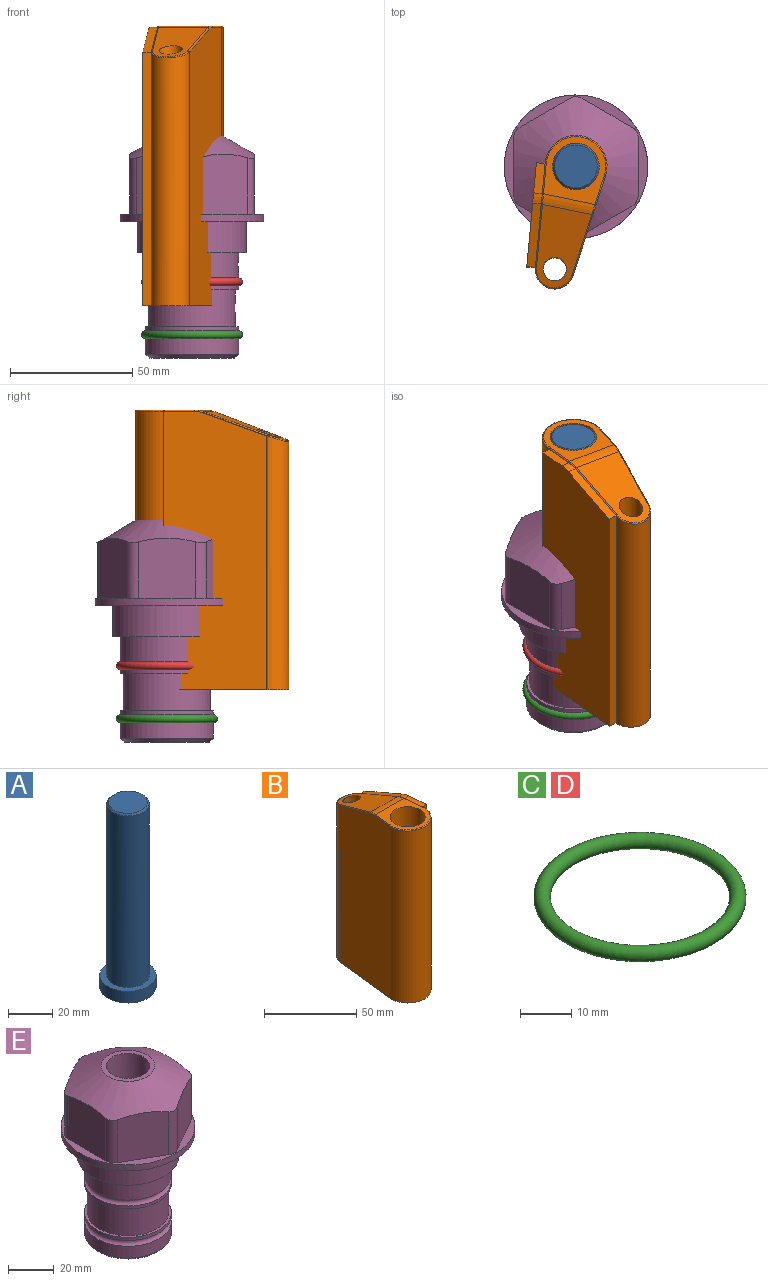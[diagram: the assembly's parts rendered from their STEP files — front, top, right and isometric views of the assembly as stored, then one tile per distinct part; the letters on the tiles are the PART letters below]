
ASSEMBLY  parts=5 mates=3
PART A: 6 faces, bbox 25.4x25.4x101.6 mm
  f0: plane 17.46x17.46mm, normal (0,0,1), area 239.5mm2, adj f5
  f1: plane 25.4x25.4mm, normal (0,0,-1), area 506.7mm2, adj f2
  f2: cylinder r=12.7mm len=25.4mm, axis (0,0,1), area 506.7mm2, adj f1,f3
  f3: plane 25.4x25.4mm, normal (0,0,1), area 221.7mm2, adj f2,f4
  f4: cylinder r=9.53mm len=94.46mm, axis (0,0,1), area 5653mm2, adj f3,f5
  f5: cone r=8.73mm half-angle=45deg, axis (0,0,-1), area 64.4mm2, adj f0,f4
PART B: 49 faces, bbox 29.9x64.5x114.4 mm
  f0: cylinder r=12.7mm len=113.87mm, axis (0,0,-1), area 4865.2mm2, adj f2,f10,f16,f47
  f1: cylinder r=7.94mm len=103.71mm, axis (0,0,-1), area 2367.2mm2, adj f2,f13,f16,f43
  f2: plane 113.87x42.33mm, normal (-0.99,0.11,0), area 4707.7mm2, adj f0,f1,f12,f14,f15,f16
  f3: cylinder r=9.53mm len=114.38mm, axis (0,0,-1), area 6845.2mm2, adj f5,f16
  f4: cylinder r=4.76mm len=106.31mm, axis (0,0,-1), area 3128.7mm2, adj f6,f16
  f5: plane 25.83x24.38mm, normal (0,0,1), area 262.2mm2, adj f3,f7,f8,f10,f12
  f6: plane 32.49x20.55mm, normal (0,0.34,0.94), area 489.9mm2, adj f4,f7,f11,f13,f15
  f7: cylinder r=12.7mm len=21.49mm, axis (-1,0,0), area 93.2mm2, adj f5,f6,f9,f14
  f8: cylinder r=0.51mm len=12.34mm, axis (0.11,-0.99,0), area 9.9mm2, adj f5,f9,f10,f46
  f9: bspline ~7.62x1.64mm, area 3.5mm2, adj f7,f8,f11,f45
  f10: torus R=12.19mm, axis (0,0,1), area 33.6mm2, adj f0,f5,f8,f12
  f11: cylinder r=0.51mm len=26.01mm, axis (0.1,-0.93,0.34), area 21.6mm2, adj f6,f9,f13,f44
  f12: cylinder r=0.51mm len=12.34mm, axis (0.11,0.99,0), area 9.9mm2, adj f2,f5,f10,f14
  f13: bspline ~15.78x7.05mm, area 15.7mm2, adj f1,f6,f11,f15
  f14: bspline ~7.62x1.64mm, area 3.5mm2, adj f2,f7,f12,f15
  f15: cylinder r=0.51mm len=26.01mm, axis (0.1,0.93,-0.34), area 21.6mm2, adj f2,f6,f13,f14
  f16: plane 63.5x28.84mm, normal (0,0,-1), area 712.4mm2, adj f0,f1,f2,f3,f4,f35,f36,f37
  f17: plane 2.3x0.95mm, normal (0,0,-1), area 1mm2, adj f19,f21,f27
  f18: plane 2.3x0.95mm, normal (0,0,-1), area 1mm2, adj f19,f25,f29
  f19: cylinder r=9.53mm len=12.93mm, axis (-1,0,0), area 37.5mm2, adj f17,f18,f20,f22,f26,f31
  f20: plane 17.94x12.32mm, normal (0,-0.34,-0.94), area 191.2mm2, adj f19,f23,f30,f33
  f21: cylinder r=1.59mm len=1.68mm, axis (0.11,0.99,0), area 2.4mm2, adj f17,f22,f24,f42
  f22: bspline ~5.82x2.33mm, area 7.7mm2, adj f19,f21,f23,f42
  f23: cylinder r=1.59mm len=18.33mm, axis (0.1,0.93,-0.34), area 46.7mm2, adj f20,f22,f34,f42
  f24: sphere r=1.59mm, area 5.4mm2, adj f21,f27,f41
  f25: torus R=14.29mm, axis (0,0,1), area 5.8mm2, adj f18,f26,f28,f40
  f26: bspline ~11.06x2.73mm, area 20.8mm2, adj f19,f25,f27,f40
  f27: torus R=14.29mm, axis (0,0,1), area 5.8mm2, adj f17,f24,f26,f40
  f28: sphere r=1.59mm, area 5.4mm2, adj f25,f29,f39
  f29: cylinder r=1.59mm len=1.68mm, axis (-0.11,0.99,0), area 2.4mm2, adj f18,f28,f31,f38
  f30: cylinder r=1.59mm len=18.33mm, axis (0.1,-0.93,0.34), area 46.7mm2, adj f20,f31,f32,f38
  f31: bspline ~5.82x2.33mm, area 7.7mm2, adj f19,f29,f30,f38
  f32: sphere r=1.59mm, area 3.6mm2, adj f30,f33,f37
  f33: bspline ~8.31x1.84mm, area 15.3mm2, adj f20,f32,f34,f36
  f34: sphere r=1.59mm, area 3.6mm2, adj f23,f33,f35
  f35: cylinder r=1.59mm len=102.61mm, axis (0,0,-1), area 311.2mm2, adj f16,f34,f36,f42
  f36: cylinder r=7.94mm len=102.95mm, axis (0,0,-1), area 736.6mm2, adj f16,f33,f35,f37
  f37: cylinder r=1.59mm len=102.61mm, axis (0,0,-1), area 311.2mm2, adj f16,f32,f36,f38
  f38: plane 109.62x21.6mm, normal (-0.99,-0.11,0), area 2314.7mm2, adj f16,f29,f30,f31,f37,f39
  f39: cylinder r=1.59mm len=109.62mm, axis (0,0,-1), area 375.8mm2, adj f16,f28,f38,f40
  f40: cylinder r=12.7mm len=109.62mm, axis (0,0,-1), area 1329.9mm2, adj f16,f25,f26,f27,f39,f41
  f41: cylinder r=1.59mm len=109.62mm, axis (0,0,-1), area 375.8mm2, adj f16,f24,f40,f42
  f42: plane 109.62x21.6mm, normal (0.99,-0.11,0), area 2314.7mm2, adj f16,f21,f22,f23,f35,f41
  f43: plane 103.71x3.52mm, normal (-0.11,0.99,0), area 366.9mm2, adj f1,f16,f44,f48
  f44: plane 26.28x9.42mm, normal (-0.04,0.34,0.94), area 98mm2, adj f11,f43,f45,f48
  f45: extruded ~4.56x3.98mm, area 15.1mm2, adj f9,f44,f46,f48
  f46: plane 12.67x4.89mm, normal (0,0,1), area 43.7mm2, adj f8,f45,f47,f48
  f47: plane 113.87x3.52mm, normal (0.11,-0.99,0), area 402.8mm2, adj f0,f16,f46,f48
  f48: plane 113.87x42.33mm, normal (0.99,0.11,0), area 4707.7mm2, adj f16,f43,f44,f45,f46,f47
PART C: 1 faces, bbox 44.7x44.7x3.2 mm
  f0: torus R=19.05mm, axis (0,0,1), area 1193.9mm2
PART D: same geometry as C
PART E: 36 faces, bbox 58.7x58.7x91.2 mm
  f0: cylinder r=17.78mm len=35.56mm, axis (0,0,1), area 1670.8mm2, adj f23,f24,f31
  f1: cylinder r=19.05mm len=38.1mm, axis (0,0,1), area 1191.9mm2, adj f26,f27,f30
  f2: plane 58.66x58.66mm, normal (0,0,-1), area 1150.6mm2, adj f3,f28
  f3: cylinder r=29.33mm len=58.66mm, axis (0,0,-1), area 585.1mm2, adj f2,f4
  f4: plane 58.66x58.66mm, normal (0,0,1), area 475.9mm2, adj f3,f5,f6,f7,f8,f9,f10,f11
  f5: plane 24.5x20.32mm, normal (-0.5,0.87,0), area 562.8mm2, adj f4,f15,f16,f17
  f6: plane 24.5x20.32mm, normal (0.5,0.87,0), area 562.8mm2, adj f4,f14,f15,f17
  f7: plane 24.5x23.48mm, normal (1,0,0), area 562.8mm2, adj f4,f13,f14,f17
  f8: plane 24.5x20.32mm, normal (0.5,-0.87,0), area 562.8mm2, adj f4,f12,f13,f17
  f9: plane 24.5x20.32mm, normal (-0.5,-0.87,0), area 562.8mm2, adj f4,f11,f12,f17
  f10: plane 24.5x23.48mm, normal (-1,0,0), area 562.8mm2, adj f4,f11,f16,f17
  f11: cylinder r=5.08mm len=23.01mm, axis (0,0,-1), area 121.2mm2, adj f4,f9,f10,f17
  f12: cylinder r=5.08mm len=23.01mm, axis (0,0,-1), area 121.2mm2, adj f4,f8,f9,f17
  f13: cylinder r=5.08mm len=23.01mm, axis (0,0,-1), area 121.2mm2, adj f4,f7,f8,f17
  f14: cylinder r=5.08mm len=23.01mm, axis (0,0,-1), area 121.2mm2, adj f4,f6,f7,f17
  f15: cylinder r=5.08mm len=23.01mm, axis (0,0,-1), area 121.2mm2, adj f4,f5,f6,f17
  f16: cylinder r=5.08mm len=23.01mm, axis (0,0,-1), area 121.2mm2, adj f4,f5,f10,f17
  f17: cone r=11.73mm half-angle=60deg, axis (0,0,-1), area 2071.8mm2, adj f5,f6,f7,f8,f9,f10,f11,f12
  f18: plane 23.46x23.46mm, normal (0,0,1), area 147.4mm2, adj f17,f35
  f19: plane 34.93x34.93mm, normal (0,0,-1), area 958mm2, adj f29
  f20: cylinder r=19.05mm len=38.1mm, axis (0,0,1), area 760.1mm2, adj f21,f29
  f21: torus R=19.05mm, axis (0,0,1), area 565.3mm2, adj f20,f22
  f22: cylinder r=19.05mm len=38.1mm, axis (0,0,1), area 190mm2, adj f21,f23
  f23: plane 38.1x38.1mm, normal (0,0,1), area 146.9mm2, adj f0,f22
  f24: plane 38.1x38.1mm, normal (0,0,-1), area 146.9mm2, adj f0,f25
  f25: cylinder r=19.05mm len=38.1mm, axis (0,0,1), area 190mm2, adj f24,f26
  f26: torus R=19.05mm, axis (0,0,1), area 565.3mm2, adj f1,f25
  f27: plane 44.45x44.45mm, normal (0,0,-1), area 411.7mm2, adj f1,f28
  f28: cylinder r=22.23mm len=44.45mm, axis (0,0,1), area 1773.5mm2, adj f2,f27
  f29: cone r=19.05mm half-angle=45deg, axis (0,0,1), area 257.5mm2, adj f19,f20
  f30: cylinder r=3.17mm len=6.75mm, axis (-1,0,0), area 128mm2, adj f1,f33
  f31: cylinder r=3.17mm len=6.35mm, axis (-1,0,0), area 102.5mm2, adj f0,f33
  f32: plane 25.4x25.4mm, normal (0,0,1), area 506.7mm2, adj f33
  f33: cylinder r=12.7mm len=66.42mm, axis (0,0,-1), area 5236.2mm2, adj f30,f31,f32,f34
  f34: cone r=9.53mm half-angle=30deg, axis (0,0,-1), area 443.4mm2, adj f33,f35
  f35: cylinder r=9.53mm len=19.05mm, axis (0,0,-1), area 849mm2, adj f18,f34
PLACE A rot(axis=(0,0,-1),101.7deg) t=(0,0,6.38)mm
PLACE B rot(axis=(0,0,1),168.3deg) t=(0,0,60.99)mm
PLACE C t=(0,0,-21.59)mm
PLACE D at identity
PLACE E at identity fixed
MATE fastened C.f0 <-> E.f0  axis (0,0,1) through (0,0,-46.1)mm
MATE cylindrical A.f2 <-> E.f0  axis (0,0,1) through (0,0,32.01)mm
MATE fastened B.f0 <-> A.f2  axis (0,0,1) through (0,0,80.04)mm
